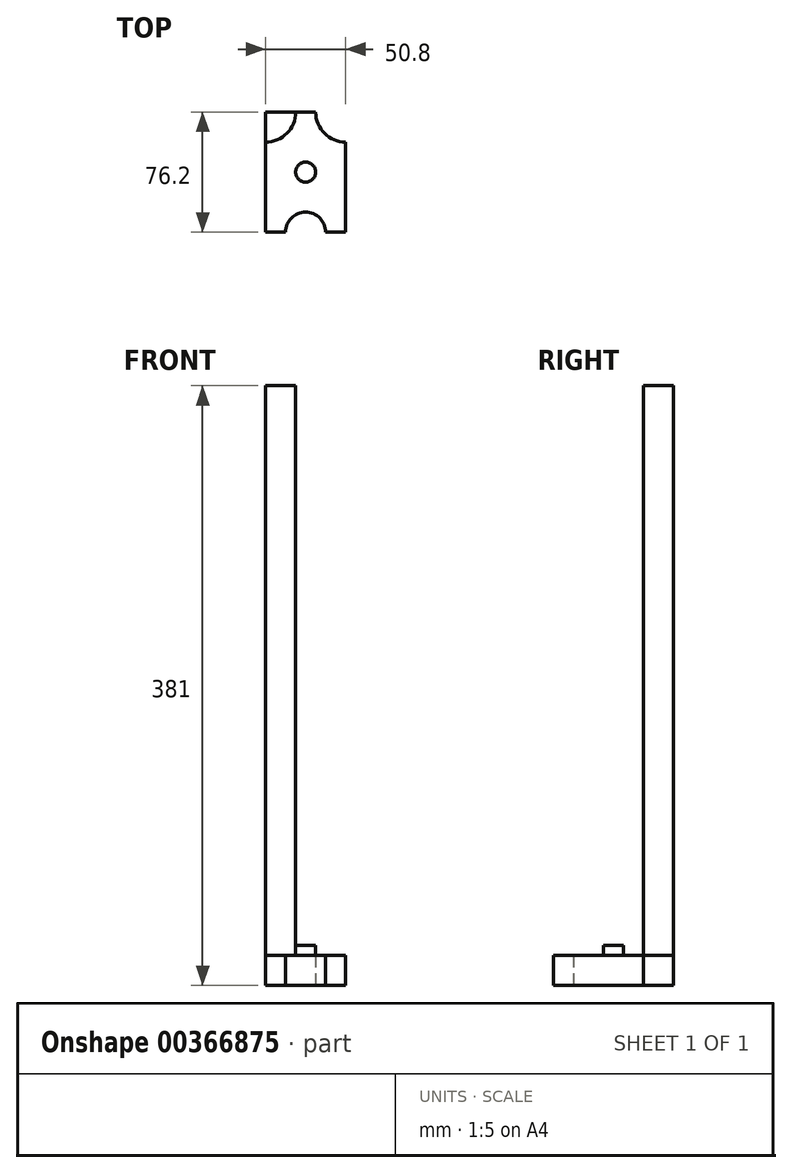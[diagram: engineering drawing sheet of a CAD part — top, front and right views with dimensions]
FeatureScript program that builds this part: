
annotation { "Feature Type Name" : "Feature", "Feature Type Description" : "" }
export const myFeature = defineFeature(function(context is Context, id is Id, definition is map)
    precondition{}
    {
        {
            assignVariable(context, id + "F0", {"name" : "Height", "anyValue" : 381 * mm});
        }
        {
            var Q0;
            Q0=qCreatedBy(makeId("Top.planeOp"),FACE);
            var sketch = newSketch(context, id + "F1", { "sketchPlane" : qUnion([Q0])});
            skLineSegment(sketch, "E0.bottom", {"start": v(25.4, 38.1) * mm, "end": v(-25.4, 38.1) * mm});
            skLineSegment(sketch, "E0.top", {"start": v(25.4, -38.1) * mm, "end": v(-25.4, -38.1) * mm});
            skLineSegment(sketch, "E0.left", {"start": v(25.4, 38.1) * mm, "end": v(25.4, -38.1) * mm});
            skLineSegment(sketch, "E0.right", {"start": v(-25.4, 38.1) * mm, "end": v(-25.4, -38.1) * mm});
            skPoint(sketch, "E0.middle", {"position": v(0, 0) * mm});
            skArc(sketch, "E1", {"start": v(-6.35, 38.1) * mm, "mid": v(-11.93, 24.63) * mm, "end": v(-25.4, 19.05) * mm});
            skArc(sketch, "E2", {"start": v(25.4, 19.05) * mm, "mid": v(11.93, 24.63) * mm, "end": v(6.35, 38.1) * mm});
            skCircle(sketch, "E3", {"center": v(0, 0) * mm, "radius": 6.35 * mm});
            skArc(sketch, "E4", {"start": v(-12.7, -38.1) * mm, "mid": v(0, -25.4) * mm, "end": v(12.7, -38.1) * mm});
            skLineSegment(sketch, "E5.bottom", {"start": v(12.7, 12.7) * mm, "end": v(-12.7, 12.7) * mm});
            skLineSegment(sketch, "E5.top", {"start": v(12.7, -12.7) * mm, "end": v(-12.7, -12.7) * mm});
            skLineSegment(sketch, "E5.left", {"start": v(12.7, 12.7) * mm, "end": v(12.7, -12.7) * mm});
            skLineSegment(sketch, "E5.right", {"start": v(-12.7, 12.7) * mm, "end": v(-12.7, -12.7) * mm});
            skSolve(sketch);
        }
        {
            var Q0;
            {var subQ2=sQuery(id+"F1.wireOp",EDGE,"E1");Q0=makeQuery(id+"F1.imprint","IMPRINT",FACE,{"disambiguationData":[TD([[makeQuery(id+"F1.imprint","IMPRINT",EDGE,{"derivedFrom":subQ2}),1.0]])]});}
            extrude(context, id + "F2", {"entities" : qUnion([Q0]), "depth" : getVariable(context, 'Height')});
        }
        {
            var Q0;
            {var subQ3=sQuery(id+"F1.wireOp",EDGE,"E2");Q0=makeQuery(id+"F1.imprint","IMPRINT",FACE,{"disambiguationData":[TD([[makeQuery(id+"F1.imprint","IMPRINT",EDGE,{"derivedFrom":subQ3}),-1.0]])]});}
            var Q1;
            {var subQ3=sQuery(id+"F1.wireOp",EDGE,"E1");Q1=makeQuery(id+"F1.imprint","IMPRINT",FACE,{"disambiguationData":[TD([[makeQuery(id+"F1.imprint","IMPRINT",EDGE,{"derivedFrom":subQ3}),-1.0]])]});}
            extrude(context, id + "F3", {"entities" : qUnion([Q0, Q1]), "operationType" : NewBodyOperationType.ADD, "depth" : 19.05 * mm});
        }
        {
            var Q0;
            {var subQ0=sQuery(id+"F1.wireOp",EDGE,"E4");Q0=makeQuery(id+"F1.imprint","IMPRINT",FACE,{"disambiguationData":[TD([[makeQuery(id+"F1.imprint","IMPRINT",EDGE,{"derivedFrom":subQ0}),-1.0]])]});}
            extrude(context, id + "F4", {"entities" : qUnion([Q0]), "operationType" : NewBodyOperationType.ADD, "depth" : 19.05 * mm});
        }
        {
            var Q0;
            Q0=makeQuery(id+"F1.imprint","IMPRINT",FACE,{"disambiguationData":[TD([[makeQuery(id+"F1.imprint","IMPRINT",EDGE,{"derivedFrom":sQuery(id+"F1.wireOp",EDGE,"E3")}),-1.0]])]});
            extrude(context, id + "F5", {"entities" : qUnion([Q0]), "operationType" : NewBodyOperationType.ADD, "depth" : 19.05 * mm});
        }
        {
            var Q0;
            Q0=makeQuery(id+"F1.imprint","IMPRINT",FACE,{"disambiguationData":[TD([[makeQuery(id+"F1.imprint","IMPRINT",EDGE,{"derivedFrom":sQuery(id+"F1.wireOp",EDGE,"E3")}),1.0]])]});
            extrude(context, id + "F6", {"entities" : qUnion([Q0]), "operationType" : NewBodyOperationType.ADD, "depth" : 25.4 * mm});
        }
        {
            var Q0;
            Q0=qCreatedBy(makeId("Top.planeOp"),FACE);
            cPlane(context, id + "F7", {"entities" : qUnion([Q0]), "cplaneType" : CPlaneType.OFFSET, "offset" : 50.8 * mm, "oppositeDirection" : true, "width" : 152.4 * mm, "height" : 152.4 * mm});
        }
    });
